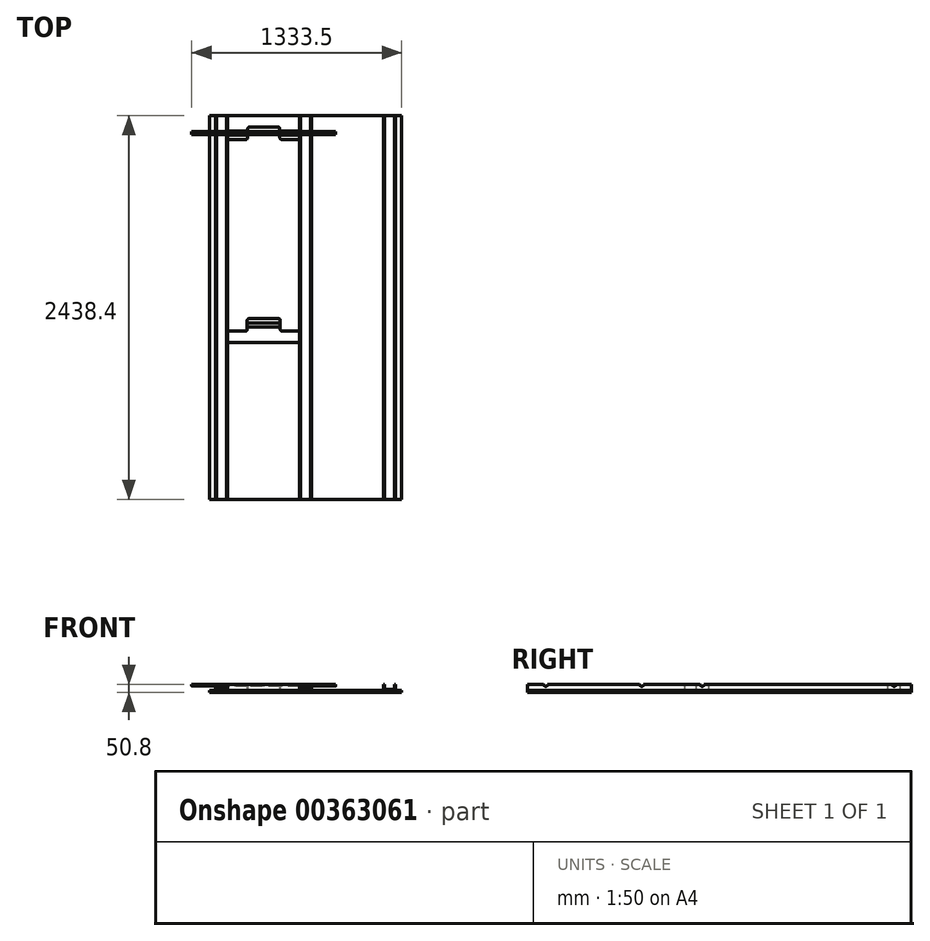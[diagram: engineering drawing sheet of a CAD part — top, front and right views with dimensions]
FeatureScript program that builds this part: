
annotation { "Feature Type Name" : "Feature", "Feature Type Description" : "" }
export const myFeature = defineFeature(function(context is Context, id is Id, definition is map)
    precondition{}
    {
        {
            var Q0;
            Q0=qCreatedBy(makeId("Top.planeOp"),FACE);
            var sketch = newSketch(context, id + "F0", { "sketchPlane" : qUnion([Q0])});
            skLineSegment(sketch, "E0.bottom", {"start": v(-609.6, 1219.2) * mm, "end": v(609.6, 1219.2) * mm});
            skLineSegment(sketch, "E0.top", {"start": v(-609.6, -1219.2) * mm, "end": v(609.6, -1219.2) * mm});
            skLineSegment(sketch, "E0.left", {"start": v(-609.6, 1219.2) * mm, "end": v(-609.6, -1219.2) * mm});
            skLineSegment(sketch, "E0.right", {"start": v(609.6, 1219.2) * mm, "end": v(609.6, -1219.2) * mm});
            skPoint(sketch, "E0.middle", {"position": v(0, 0) * mm});
            skSolve(sketch);
        }
        {
            var Q0;
            Q0=qSketchRegion(id+"F0",true);
            extrude(context, id + "F1", {"entities" : qUnion([Q0]), "depth" : 12.7 * mm});
        }
        {
            var Q0;
            Q0=qCreatedBy(makeId("Front.planeOp"),FACE);
            var sketch = newSketch(context, id + "F2", { "sketchPlane" : qUnion([Q0])});
            skLineSegment(sketch, "E1.bottom", {"start": v(38.1, 88.9) * mm, "end": v(-38.1, 88.9) * mm});
            skLineSegment(sketch, "E1.top", {"start": v(38.1, 12.7) * mm, "end": v(-38.1, 12.7) * mm});
            skLineSegment(sketch, "E1.left", {"start": v(38.1, 88.9) * mm, "end": v(38.1, 12.7) * mm});
            skLineSegment(sketch, "E1.right", {"start": v(-38.1, 88.9) * mm, "end": v(-38.1, 12.7) * mm});
            skPoint(sketch, "E1.middle", {"position": v(0, 50.8) * mm});
            skLineSegment(sketch, "E2.bottom", {"start": v(31.75, 82.55) * mm, "end": v(-31.75, 82.55) * mm});
            skLineSegment(sketch, "E2.top", {"start": v(31.75, 19.05) * mm, "end": v(-31.75, 19.05) * mm});
            skLineSegment(sketch, "E2.left", {"start": v(31.75, 82.55) * mm, "end": v(31.75, 19.05) * mm});
            skLineSegment(sketch, "E2.right", {"start": v(-31.75, 82.55) * mm, "end": v(-31.75, 19.05) * mm});
            skLineSegment(sketch, "E3.bottom", {"start": v(-495.3, 88.9) * mm, "end": v(-571.5, 88.9) * mm});
            skLineSegment(sketch, "E3.top", {"start": v(-495.3, 12.7) * mm, "end": v(-571.5, 12.7) * mm});
            skLineSegment(sketch, "E3.left", {"start": v(-495.3, 88.9) * mm, "end": v(-495.3, 12.7) * mm});
            skLineSegment(sketch, "E3.right", {"start": v(-571.5, 88.9) * mm, "end": v(-571.5, 12.7) * mm});
            skPoint(sketch, "E3.middle", {"position": v(-533.4, 50.8) * mm});
            skLineSegment(sketch, "E4.bottom", {"start": v(571.5, 88.9) * mm, "end": v(495.3, 88.9) * mm});
            skLineSegment(sketch, "E4.top", {"start": v(571.5, 12.7) * mm, "end": v(495.3, 12.7) * mm});
            skLineSegment(sketch, "E4.left", {"start": v(571.5, 88.9) * mm, "end": v(571.5, 12.7) * mm});
            skLineSegment(sketch, "E4.right", {"start": v(495.3, 88.9) * mm, "end": v(495.3, 12.7) * mm});
            skPoint(sketch, "E4.middle", {"position": v(533.4, 50.8) * mm});
            skLineSegment(sketch, "E5.bottom", {"start": v(-565.15, 82.55) * mm, "end": v(-501.65, 82.55) * mm});
            skLineSegment(sketch, "E5.top", {"start": v(-565.15, 19.05) * mm, "end": v(-501.65, 19.05) * mm});
            skLineSegment(sketch, "E5.left", {"start": v(-565.15, 82.55) * mm, "end": v(-565.15, 19.05) * mm});
            skLineSegment(sketch, "E5.right", {"start": v(-501.65, 82.55) * mm, "end": v(-501.65, 19.05) * mm});
            skLineSegment(sketch, "E6.bottom", {"start": v(501.65, 82.55) * mm, "end": v(565.15, 82.55) * mm});
            skLineSegment(sketch, "E6.top", {"start": v(501.65, 19.05) * mm, "end": v(565.15, 19.05) * mm});
            skLineSegment(sketch, "E6.left", {"start": v(501.65, 82.55) * mm, "end": v(501.65, 19.05) * mm});
            skLineSegment(sketch, "E6.right", {"start": v(565.15, 82.55) * mm, "end": v(565.15, 19.05) * mm});
            skSolve(sketch);
        }
        {
            var Q0;
            Q0=qSketchRegion(id+"F2",true);
            extrude(context, id + "F3", {"entities" : qUnion([Q0]), "endBound" : BoundingType.SYMMETRIC, "depth" : 2438.4 * mm});
        }
        {
            var Q0;
            Q0=makeQuery(id+"F1.opExtrude","CAP_FACE",FACE,{"disambiguationData":[OSD([sQuery(id+"F0.wireOp",EDGE,"E0.bottom"),sQuery(id+"F0.wireOp",EDGE,"E0.top"),sQuery(id+"F0.wireOp",EDGE,"E0.left"),sQuery(id+"F0.wireOp",EDGE,"E0.right")])],"isStart":false});
            var sketch = newSketch(context, id + "F4", { "sketchPlane" : qUnion([Q0])});
            skLineSegment(sketch, "E7.0", {"start": v(-495.3, -1219.2) * mm, "end": v(-495.3, 1219.2) * mm});
            skLineSegment(sketch, "E8.0", {"start": v(-38.1, -1219.2) * mm, "end": v(-38.1, 1219.2) * mm});
            skLineSegment(sketch, "E9.0", {"start": v(38.1, -1219.2) * mm, "end": v(38.1, 1219.2) * mm});
            skLineSegment(sketch, "E10.0", {"start": v(495.3, -1219.2) * mm, "end": v(495.3, 1219.2) * mm});
            skLineSegment(sketch, "E11", {"start": v(-495.3, 1066.8) * mm, "end": v(-368.3, 1066.8) * mm});
            skLineSegment(sketch, "E12", {"start": v(-368.3, 1066.8) * mm, "end": v(-368.3, 1146.18) * mm});
            skLineSegment(sketch, "E13", {"start": v(-368.3, 1146.18) * mm, "end": v(-165.1, 1146.18) * mm});
            skLineSegment(sketch, "E14", {"start": v(-165.1, 1146.18) * mm, "end": v(-165.1, 1066.8) * mm});
            skLineSegment(sketch, "E15", {"start": v(-165.1, 1066.8) * mm, "end": v(-38.1, 1066.8) * mm});
            skLineSegment(sketch, "E16", {"start": v(-495.3, 1219.2) * mm, "end": v(-38.1, 1219.2) * mm});
            skLineSegment(sketch, "E17", {"start": v(-495.3, -1219.2) * mm, "end": v(-38.1, -1219.2) * mm});
            skLineSegment(sketch, "E18", {"start": v(0, 1288.87) * mm, "end": v(0, -1353.9) * mm, "construction": true});
            skPoint(sketch, "E18.startSnap0", {"position": v(0, 1219.2) * mm});
            skLineSegment(sketch, "E19", {"start": v(-495.3, -149.23) * mm, "end": v(-371.48, -149.23) * mm});
            skLineSegment(sketch, "E20", {"start": v(-371.48, -149.23) * mm, "end": v(-371.48, -69.85) * mm});
            skLineSegment(sketch, "E21", {"start": v(-371.48, -69.85) * mm, "end": v(-161.93, -69.85) * mm});
            skLineSegment(sketch, "E22", {"start": v(-161.93, -69.85) * mm, "end": v(-161.93, -149.23) * mm});
            skLineSegment(sketch, "E23", {"start": v(-161.93, -149.23) * mm, "end": v(-38.1, -149.23) * mm});
            skLineSegment(sketch, "E24", {"start": v(-38.1, -222.25) * mm, "end": v(-495.3, -222.25) * mm});
            skLineSegment(sketch, "E25", {"start": v(-368.3, 1108.07) * mm, "end": v(-165.1, 1108.07) * mm, "construction": true});
            skLineSegment(sketch, "E26", {"start": v(-371.48, -111.13) * mm, "end": v(-161.93, -111.13) * mm, "construction": true});
            skSolve(sketch);
        }
        {
            var Q0;
            {var subQ0=sQuery(id+"F4.wireOp",EDGE,"E11");Q0=makeQuery(id+"F4.imprint","IMPRINT",FACE,{"disambiguationData":[TD([[makeQuery(id+"F4.imprint","IMPRINT",EDGE,{"derivedFrom":subQ0}),1.0]])]});}
            var Q1;
            {var subQ0=sQuery(id+"F4.wireOp",EDGE,"E19");Q1=makeQuery(id+"F4.imprint","IMPRINT",FACE,{"disambiguationData":[TD([[makeQuery(id+"F4.imprint","IMPRINT",EDGE,{"derivedFrom":subQ0}),-1.0]])]});}
            var Q2;
            Q2=makeQuery(id+"F3.opExtrude","SWEPT_FACE",FACE,{"disambiguationData":[OSD([sQuery(id+"F2.wireOp",EDGE,"E3.bottom")])]});
            extrude(context, id + "F5", {"entities" : qUnion([Q0, Q1]), "endBound" : BoundingType.UP_TO_SURFACE, "endBoundEntityFace" : qUnion([Q2]), "depth" : 25.4 * mm});
        }
        {
            var Q0;
            Q0=qCreatedBy(makeId("Right.planeOp"),FACE);
            var sketch = newSketch(context, id + "F6", { "sketchPlane" : qUnion([Q0])});
            skCircle(sketch, "E27", {"center": v(1108.08, 50.8) * mm, "radius": 12.7 * mm});
            skCircle(sketch, "E28", {"center": v(-111.12, 50.8) * mm, "radius": 12.7 * mm});
            skCircle(sketch, "E29", {"center": v(-495.3, 50.8) * mm, "radius": 12.7 * mm});
            skCircle(sketch, "E30", {"center": v(-1104.9, 50.8) * mm, "radius": 12.7 * mm});
            skSolve(sketch);
        }
        {
            var Q0;
            Q0=qSketchRegion(id+"F6",true);
            extrude(context, id + "F7", {"entities" : qUnion([Q0]), "operationType" : NewBodyOperationType.REMOVE, "endBound" : BoundingType.SYMMETRIC, "depth" : 1219.2 * mm});
        }
        {
            var Q0;
            Q0=makeQuery(id+"F5.opExtrude","SWEPT_EDGE",EDGE,{"disambiguationData":[OSD([sQuery(id+"F4.wireOp",EDGE,"E13"),sQuery(id+"F4.wireOp",EDGE,"E14")])]});
            var Q1;
            Q1=makeQuery(id+"F5.opExtrude","SWEPT_EDGE",EDGE,{"disambiguationData":[OSD([sQuery(id+"F4.wireOp",EDGE,"E12"),sQuery(id+"F4.wireOp",EDGE,"E13")])]});
            var Q2;
            Q2=makeQuery(id+"F5.opExtrude","SWEPT_EDGE",EDGE,{"disambiguationData":[OSD([sQuery(id+"F4.wireOp",EDGE,"E19"),sQuery(id+"F4.wireOp",EDGE,"E20")])]});
            var Q3;
            Q3=makeQuery(id+"F5.opExtrude","SWEPT_EDGE",EDGE,{"disambiguationData":[OSD([sQuery(id+"F4.wireOp",EDGE,"E22"),sQuery(id+"F4.wireOp",EDGE,"E23")])]});
            fillet(context, id + "F8", {"entities" : qUnion([Q0, Q1, Q2, Q3]), "radius" : 9.52 * mm, "tangentPropagation" : true, "allowEdgeOverflow" : false});
        }
        {
            var Q0;
            Q0=makeQuery(id+"F5.opExtrude","SWEPT_EDGE",EDGE,{"disambiguationData":[OSD([sQuery(id+"F4.wireOp",EDGE,"E21"),sQuery(id+"F4.wireOp",EDGE,"E22")])]});
            var Q1;
            Q1=makeQuery(id+"F5.opExtrude","SWEPT_EDGE",EDGE,{"disambiguationData":[OSD([sQuery(id+"F4.wireOp",EDGE,"E20"),sQuery(id+"F4.wireOp",EDGE,"E21")])]});
            var Q2;
            Q2=makeQuery(id+"F5.opExtrude","SWEPT_EDGE",EDGE,{"disambiguationData":[OSD([sQuery(id+"F4.wireOp",EDGE,"E14"),sQuery(id+"F4.wireOp",EDGE,"E15")])]});
            var Q3;
            Q3=makeQuery(id+"F5.opExtrude","SWEPT_EDGE",EDGE,{"disambiguationData":[OSD([sQuery(id+"F4.wireOp",EDGE,"E11"),sQuery(id+"F4.wireOp",EDGE,"E12")])]});
            fillet(context, id + "F9", {"entities" : qUnion([Q0, Q1, Q2, Q3]), "radius" : 12.7 * mm, "tangentPropagation" : true, "allowEdgeOverflow" : false});
        }
        {
            var Q0;
            Q0=makeQuery(id+"F3.opExtrude","SWEPT_FACE",FACE,{"disambiguationData":[OSD([sQuery(id+"F2.wireOp",EDGE,"E3.left")])]});
            cPlane(context, id + "F10", {"entities" : qUnion([Q0]), "cplaneType" : CPlaneType.OFFSET, "offset" : 228.6 * mm, "width" : 152.4 * mm, "height" : 152.4 * mm});
        }
        {
            var Q0;
            Q0=qCreatedBy(id+"F10.planeOp",FACE);
            var sketch = newSketch(context, id + "F11", { "sketchPlane" : qUnion([Q0])});
            skCircle(sketch, "E31.0", {"center": v(1108.08, 50.8) * mm, "radius": 12.7 * mm});
            skCircle(sketch, "E32", {"center": v(1108.08, 50.8) * mm, "radius": 10.67 * mm});
            skSolve(sketch);
        }
        {
            var Q0;
            Q0=makeQuery(id+"F11.imprint","IMPRINT",FACE,{"disambiguationData":[TD([[makeQuery(id+"F11.imprint","IMPRINT",EDGE,{"derivedFrom":sQuery(id+"F11.wireOp",EDGE,"E32")}),1.0]])]});
            extrude(context, id + "F12", {"entities" : qUnion([Q0]), "endBound" : BoundingType.SYMMETRIC, "depth" : 914.4 * mm});
        }
        {
            var Q0;
            Q0=makeQuery(id+"F1.opExtrude","CAP_FACE",FACE,{"disambiguationData":[OSD([sQuery(id+"F0.wireOp",EDGE,"E0.bottom"),sQuery(id+"F0.wireOp",EDGE,"E0.top"),sQuery(id+"F0.wireOp",EDGE,"E0.left"),sQuery(id+"F0.wireOp",EDGE,"E0.right")])],"isStart":false});
            cPlane(context, id + "F13", {"entities" : qUnion([Q0]), "cplaneType" : CPlaneType.OFFSET, "offset" : 38.1 * mm, "width" : 152.4 * mm, "height" : 152.4 * mm});
        }
        {
            var Q0;
            Q0=qCreatedBy(id+"F13.planeOp",FACE);
            var sketch = newSketch(context, id + "F14", { "sketchPlane" : qUnion([Q0])});
            skLineSegment(sketch, "E33.bottom", {"start": v(725.78, 1411.34) * mm, "end": v(-725.78, 1411.34) * mm});
            skLineSegment(sketch, "E33.top", {"start": v(725.78, -1411.34) * mm, "end": v(-725.78, -1411.34) * mm});
            skLineSegment(sketch, "E33.left", {"start": v(725.78, 1411.34) * mm, "end": v(725.78, -1411.34) * mm});
            skLineSegment(sketch, "E33.right", {"start": v(-725.78, 1411.34) * mm, "end": v(-725.78, -1411.34) * mm});
            skPoint(sketch, "E33.middle", {"position": v(0, 0) * mm});
            skSolve(sketch);
        }
        {
            var Q0;
            Q0=qSketchRegion(id+"F14",true);
            extrude(context, id + "F15", {"entities" : qUnion([Q0]), "operationType" : NewBodyOperationType.REMOVE, "endBound" : BoundingType.THROUGH_ALL, "depth" : 25.4 * mm, "offsetDistance" : 25.4 * mm});
        }
        {
            var Q0;
            Q0=qCreatedBy(id+"F10.planeOp",FACE);
            cPlane(context, id + "F16", {"entities" : qUnion([Q0]), "cplaneType" : CPlaneType.OFFSET, "offset" : 165.1 * mm, "width" : 152.4 * mm, "height" : 152.4 * mm});
        }
    });
